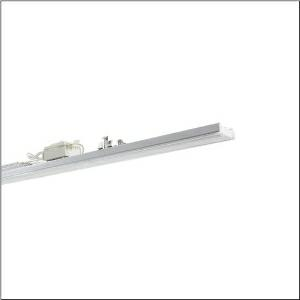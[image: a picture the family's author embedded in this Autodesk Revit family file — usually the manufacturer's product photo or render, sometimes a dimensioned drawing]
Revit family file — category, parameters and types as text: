
# Revit family: licross_r__11_recessed_ho_51te1edv4lxs_78b0
name_source: partatom
category: Lighting Fixtures
units: mm (PartAtom-declared; Revit-internal decimal feet)

## family parameters
Cut with Voids When Loaded = No
Host = Face
Light Source = No
Part Type = Normal
Room Calculation Point = No
Round Connector Dimension = Use Diameter
Shared = No

## types (1)
- --- (1 x LED, 20440 lm, 111.8 W, 4000K)
    Apparent Load = 112 VA
    CIE Flux Codes = 85 95 99 100 100
    Color Rendering = 80
    Color Temperature = 4000K
    Default Elevation = 1800 mm
    Description = Licross® 11 Recessed HO, luminaire insert, of sheet steel, galvanised, coil coated, white, length: 2.250mm, width: 66mm, height: 67mm, LED rated luminous flux: 20.440lm, light colour: 840, control gear: DALI 2, with plug, 5-pole, with phase selection, mains connection: 220..240V, AC, 50/60Hz, rated input power: 112W, halogen-free wiring, primary light control with lens, of plastic, primary optical cover: cover, of PMMA, light emission: direct distribution, primary light characteristic: symmetric, protection rating (complete): IP54, insulation class (complete): insulation class I (protective earthing), certification: CE, ENEC, VDE, UKCA, protection symbol: D if used in an environment with non-conductive dust loads with corresponding accessories, impact resistance: IK06, permissible ambient temperature for indoor applications: -40..+45°C, corresponds to IFS (International Featured Standards) requirements for safety and quality in the food industry, reducing of maximum allowable ambient temperature of 5°C with ceiling mounting, LABS conformity tested according to VDMA 24364:2018-05, packaging unit: 1 piece
    Height = 58 mm
    Lamp = 1 x LED
    Lamp Light Flux = 20440 lm
    Lamp Power = 111.8 W
    Lamp count = 1
    Length = 2250 mm
    Luminous efficacy = 183 lm/W
    Manufacturer = Siteco
    ModVariant = No
    Model = 51TE1EDV4LXS
    Mounting Place = Ceiling
    Mounting Type = Pendant
    Number of Poles = 1
    OnlyDefault = Yes
    Power Factor = 1
    Product Name = Licross® 11 Recessed HO
    Product group = luminaire insert
    ProductGroupID = 902
    Protection Class = Protection class I
    Protection Degree = IP 54
    RLX_Detail_Level = 1
    RLX_Emergency_Light_Flux = 0 lm
    RLX_Emergency_Type = 0
    RLX_Emergency_Type_DB = No
    RlxData = <blob elided: 29677 chars, md5=8d350684>
    Socket = socket
    Standby Power = 0 W
    System Light Flux = 20440 lm
    System Power = 112 W
    Type Comments = factory setting: luminous flux: 100 % | dim-lin: 254 | 520 mA
    Type Image = l_1296930.jpg
    URL = http://relux.com
    VarID = @adj_095630
    Voltage = 0 V
    Weight = 0.00 kg
    Width = 66 mm

## geometry (parser evidence)
native form markers: Blend x4, Sweep x9
no freeform markers — native parametric forms only
